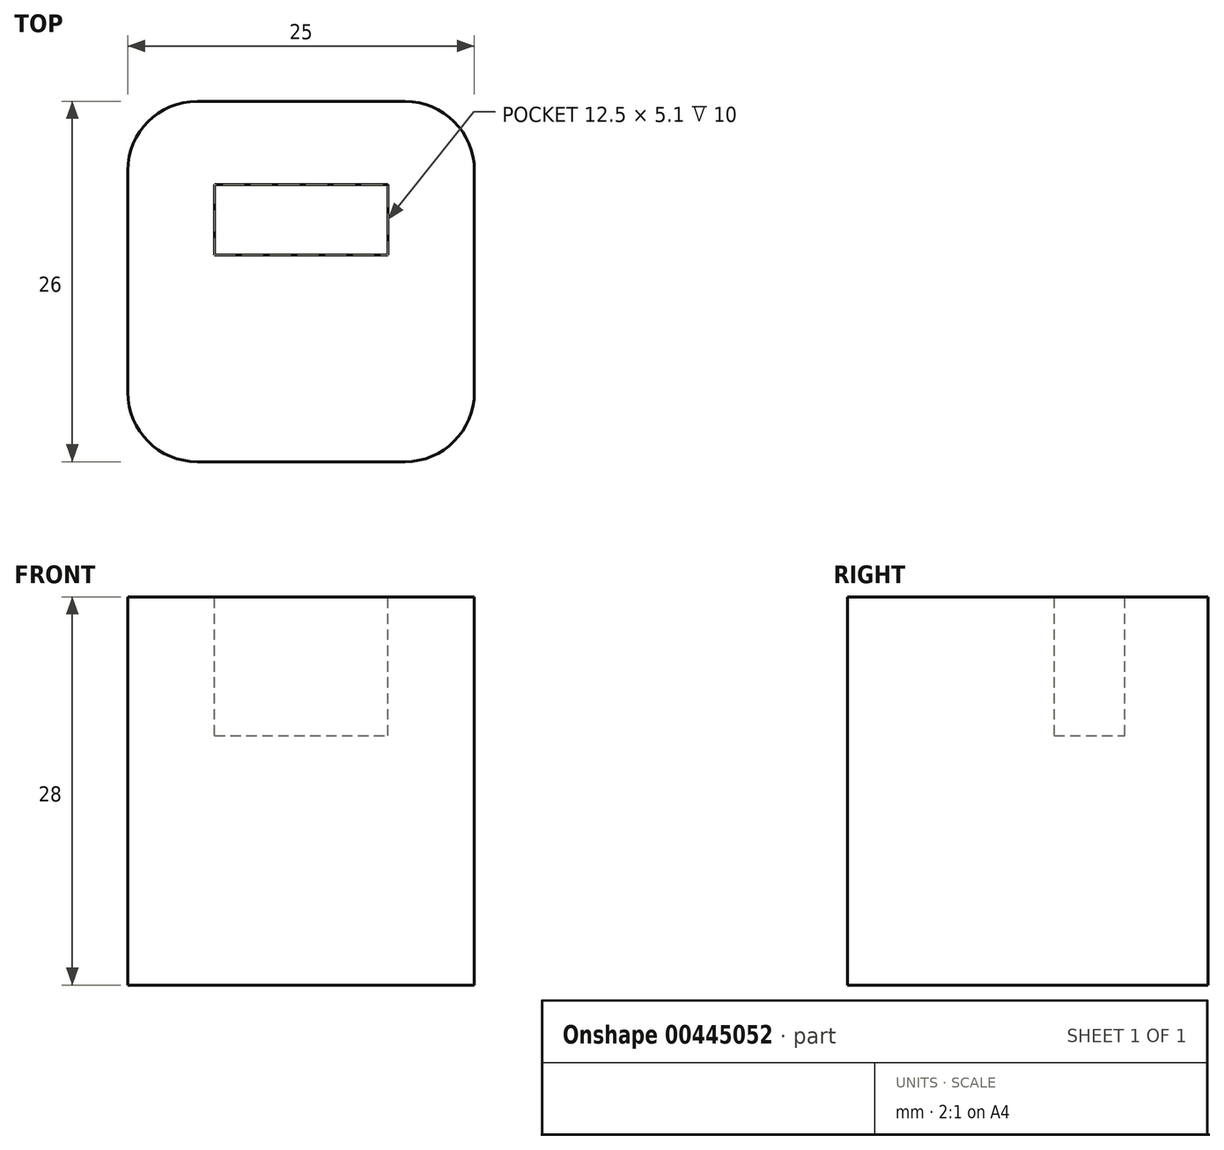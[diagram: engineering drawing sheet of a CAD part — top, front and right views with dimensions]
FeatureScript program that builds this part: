
annotation { "Feature Type Name" : "Feature", "Feature Type Description" : "" }
export const myFeature = defineFeature(function(context is Context, id is Id, definition is map)
    precondition{}
    {
        {
            var Q0;
            Q0=qCreatedBy(makeId("Top.planeOp"),FACE);
            var sketch = newSketch(context, id + "F0", { "sketchPlane" : qUnion([Q0])});
            skLineSegment(sketch, "E0.bottom", {"start": v(5, 0) * mm, "end": v(20, 0) * mm});
            skLineSegment(sketch, "E0.top", {"start": v(5, 26) * mm, "end": v(20, 26) * mm});
            skLineSegment(sketch, "E0.left", {"start": v(0, 5) * mm, "end": v(0, 21) * mm});
            skLineSegment(sketch, "E0.right", {"start": v(25, 5) * mm, "end": v(25, 21) * mm});
            skPoint(sketch, "E1.visualSharp", {"position": v(0, 26) * mm});
            skArc(sketch, "E1.filletArc", {"start": v(5, 26) * mm, "mid": v(1.46, 24.54) * mm, "end": v(0, 21) * mm});
            skPoint(sketch, "E2.visualSharp", {"position": v(25, 26) * mm});
            skArc(sketch, "E2.filletArc", {"start": v(25, 21) * mm, "mid": v(23.54, 24.54) * mm, "end": v(20, 26) * mm});
            skPoint(sketch, "E3.visualSharp", {"position": v(25, 0) * mm});
            skArc(sketch, "E3.filletArc", {"start": v(20, 0) * mm, "mid": v(23.54, 1.46) * mm, "end": v(25, 5) * mm});
            skPoint(sketch, "E4.visualSharp", {"position": v(0, 0) * mm});
            skArc(sketch, "E4.filletArc", {"start": v(0, 5) * mm, "mid": v(1.46, 1.46) * mm, "end": v(5, 0) * mm});
            skSolve(sketch);
        }
        {
            var Q0;
            Q0=makeQuery(id+"F0.imprint","IMPRINT",FACE,{"disambiguationData":[TD([[makeQuery(id+"F0.imprint","IMPRINT",EDGE,{"derivedFrom":sQuery(id+"F0.wireOp",EDGE,"E0.bottom")}),1.0]])]});
            extrude(context, id + "F1", {"entities" : qUnion([Q0]), "depth" : 28 * mm});
        }
        {
            var Q0;
            Q0=makeQuery(id+"F1.opExtrude","CAP_FACE",FACE,{"disambiguationData":[OSD([sQuery(id+"F0.wireOp",EDGE,"E0.bottom"),sQuery(id+"F0.wireOp",EDGE,"E0.top"),sQuery(id+"F0.wireOp",EDGE,"E0.left"),sQuery(id+"F0.wireOp",EDGE,"E0.right"),sQuery(id+"F0.wireOp",EDGE,"E1.filletArc"),sQuery(id+"F0.wireOp",EDGE,"E2.filletArc"),sQuery(id+"F0.wireOp",EDGE,"E3.filletArc"),sQuery(id+"F0.wireOp",EDGE,"E4.filletArc")])],"isStart":false});
            var sketch = newSketch(context, id + "F2", { "sketchPlane" : qUnion([Q0])});
            skLineSegment(sketch, "E5.bottom", {"start": v(6.25, 14.9) * mm, "end": v(18.75, 14.9) * mm});
            skLineSegment(sketch, "E5.top", {"start": v(6.25, 20) * mm, "end": v(18.75, 20) * mm});
            skLineSegment(sketch, "E5.left", {"start": v(6.25, 14.9) * mm, "end": v(6.25, 20) * mm});
            skLineSegment(sketch, "E5.right", {"start": v(18.75, 14.9) * mm, "end": v(18.75, 20) * mm});
            skPoint(sketch, "E6", {"position": v(12.5, 20) * mm});
            skSolve(sketch);
        }
        {
            var Q0;
            Q0 = qSketchRegion(id + "F2", true);
            extrude(context, id + "F3", {"entities" : qUnion([Q0]), "operationType" : NewBodyOperationType.REMOVE, "oppositeDirection" : true, "depth" : 10 * mm});
        }
    });
